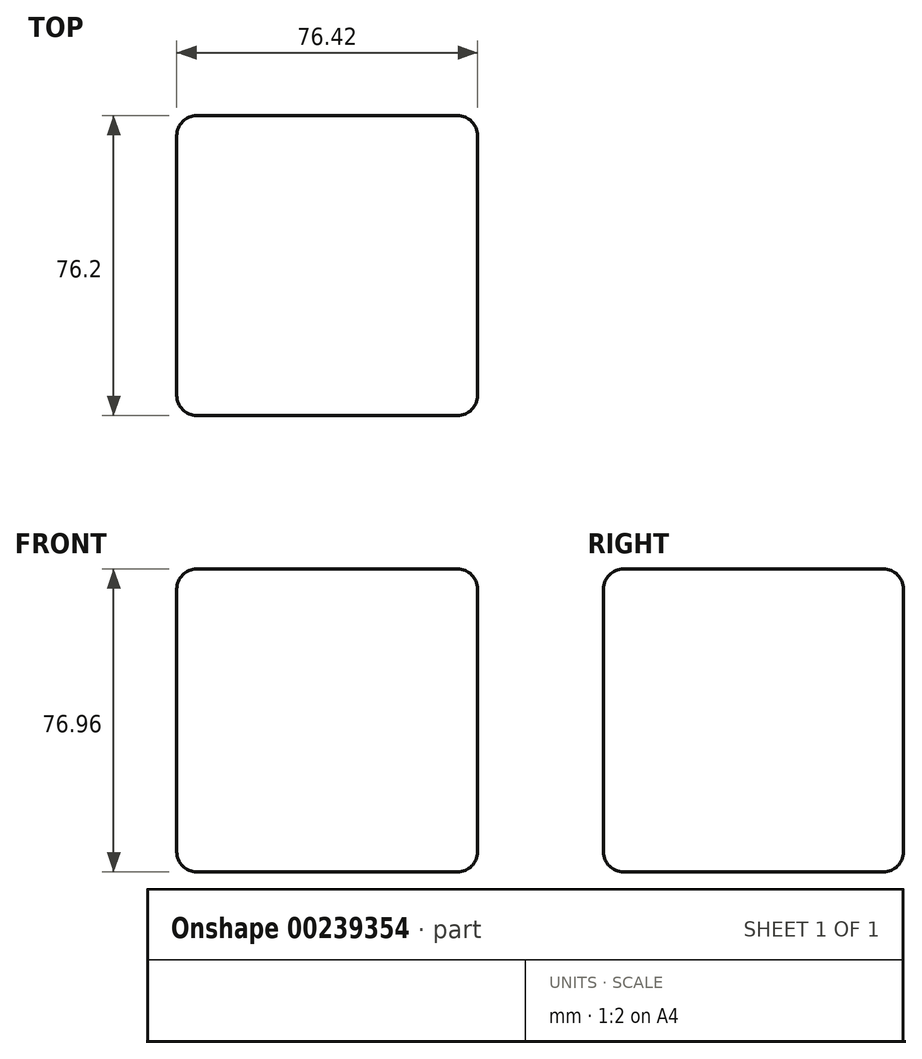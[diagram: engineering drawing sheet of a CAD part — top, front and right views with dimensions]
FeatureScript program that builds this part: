
annotation { "Feature Type Name" : "Feature", "Feature Type Description" : "" }
export const myFeature = defineFeature(function(context is Context, id is Id, definition is map)
    precondition{}
    {
        {
            var Q0;
            Q0=qCreatedBy(makeId("Front.planeOp"),FACE);
            var sketch = newSketch(context, id + "F0", { "sketchPlane" : qUnion([Q0])});
            skLineSegment(sketch, "E0.bottom", {"start": v(-38.2, 38.48) * mm, "end": v(38.2, 38.48) * mm});
            skLineSegment(sketch, "E0.top", {"start": v(-38.2, -38.48) * mm, "end": v(38.2, -38.48) * mm});
            skLineSegment(sketch, "E0.left", {"start": v(-38.2, 38.48) * mm, "end": v(-38.2, -38.48) * mm});
            skLineSegment(sketch, "E0.right", {"start": v(38.2, 38.48) * mm, "end": v(38.2, -38.48) * mm});
            skPoint(sketch, "E0.middle", {"position": v(0, 0) * mm});
            skSolve(sketch);
        }
        {
            var Q0;
            Q0=qSketchRegion(id+"F0",true);
            extrude(context, id + "F1", {"entities" : qUnion([Q0]), "depth" : 38.1 * mm, "hasSecondDirection" : true, "secondDirectionOppositeDirection" : true, "secondDirectionDepth" : 38.1 * mm});
        }
        {
            var Q0;
            Q0=makeQuery(id+"F1.opExtrude","SWEPT_EDGE",EDGE,{"disambiguationData":[OSD([sQuery(id+"F0.wireOp",EDGE,"E0.bottom"),sQuery(id+"F0.wireOp",EDGE,"E0.right")])]});
            var Q1;
            Q1=makeQuery(id+"F1.opExtrude","CAP_EDGE",EDGE,{"disambiguationData":[OSD([sQuery(id+"F0.wireOp",EDGE,"E0.bottom")])],"isStart":true});
            var Q2;
            Q2=makeQuery(id+"F1.opExtrude","CAP_EDGE",EDGE,{"disambiguationData":[OSD([sQuery(id+"F0.wireOp",EDGE,"E0.right")])],"isStart":true});
            var Q3;
            Q3=makeQuery(id+"F1.opExtrude","SWEPT_EDGE",EDGE,{"disambiguationData":[OSD([sQuery(id+"F0.wireOp",EDGE,"E0.top"),sQuery(id+"F0.wireOp",EDGE,"E0.right")])]});
            var Q4;
            Q4=makeQuery(id+"F1.opExtrude","CAP_FACE",FACE,{"disambiguationData":[OSD([sQuery(id+"F0.wireOp",EDGE,"E0.bottom"),sQuery(id+"F0.wireOp",EDGE,"E0.top"),sQuery(id+"F0.wireOp",EDGE,"E0.left"),sQuery(id+"F0.wireOp",EDGE,"E0.right")])],"isStart":true});
            var Q5;
            Q5=makeQuery(id+"F1.opExtrude","CAP_FACE",FACE,{"disambiguationData":[OSD([sQuery(id+"F0.wireOp",EDGE,"E0.bottom"),sQuery(id+"F0.wireOp",EDGE,"E0.top"),sQuery(id+"F0.wireOp",EDGE,"E0.left"),sQuery(id+"F0.wireOp",EDGE,"E0.right")])],"isStart":false});
            var Q6;
            Q6=makeQuery(id+"F1.opExtrude","SWEPT_FACE",FACE,{"disambiguationData":[OSD([sQuery(id+"F0.wireOp",EDGE,"E0.left")])]});
            fillet(context, id + "F2", {"entities" : qUnion([Q0, Q1, Q2, Q3, Q4, Q5, Q6]), "radius" : 5.08 * mm, "tangentPropagation" : true, "allowEdgeOverflow" : false});
        }
    });
